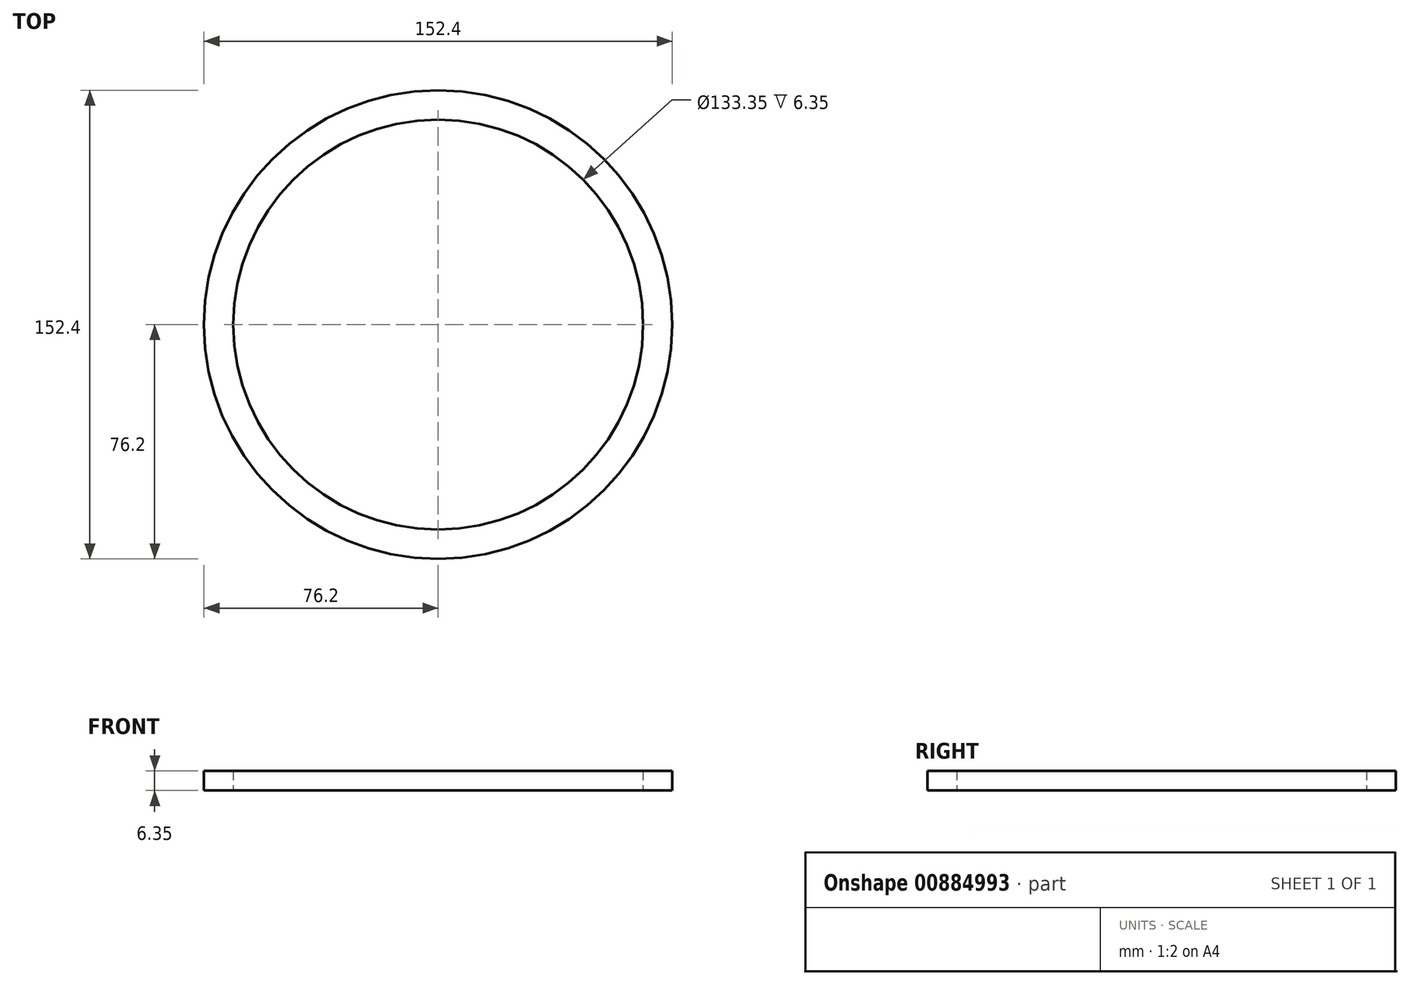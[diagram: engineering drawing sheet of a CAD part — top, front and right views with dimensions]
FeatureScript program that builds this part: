
annotation { "Feature Type Name" : "Feature", "Feature Type Description" : "" }
export const myFeature = defineFeature(function(context is Context, id is Id, definition is map)
    precondition{}
    {
        {
            var Q0;
            Q0=qCreatedBy(makeId("Top.planeOp"),FACE);
            var sketch = newSketch(context, id + "F0", { "sketchPlane" : qUnion([Q0])});
            skCircle(sketch, "E0", {"center": v(0, 0) * mm, "radius": 66.68 * mm});
            skCircle(sketch, "E1", {"center": v(0, 0) * mm, "radius": 76.2 * mm});
            skSolve(sketch);
        }
        {
            var Q0;
            Q0=makeQuery(id+"F0.imprint","IMPRINT",FACE,{"disambiguationData":[TD([[makeQuery(id+"F0.imprint","IMPRINT",EDGE,{"derivedFrom":sQuery(id+"F0.wireOp",EDGE,"E0")}),-1.0]])]});
            extrude(context, id + "F1", {"entities" : qUnion([Q0]), "depth" : 6.35 * mm, "offsetDistance" : 25.4 * mm});
        }
    });
